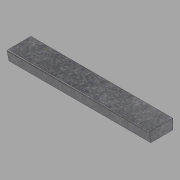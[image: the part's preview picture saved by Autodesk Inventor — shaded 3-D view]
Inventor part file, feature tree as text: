
AUTODESK INVENTOR PART (.ipt)
format: ipt  version: 2022.1 (Build 261234020, 234B)  size: 117,248 bytes
history: native  units: in
note: dims shown in document units (in); Inventor stores cm internally (conversion verified against a paired STEP export)
features: other x3, extrude x1, sketch x1
ambient origin geometry x8: Origin, YZ Plane, XZ Plane, XY Plane, X Axis, Y Axis, Z Axis, Center Point
bodies: Solid1 (feature_tree)
feature tree (5):
  other  "Blocks"
  extrude  "Extrusion1"  Depth=83.625in TaperAngle=0.0deg
  sketch  "Sketch1"  dims[d0=13.0in d1=6.0in d2=13.5in d3=0.5in d4=0.5in d5=83.625in d6=0.0in]
  other  "Profile"
  other  "Profile:1"
